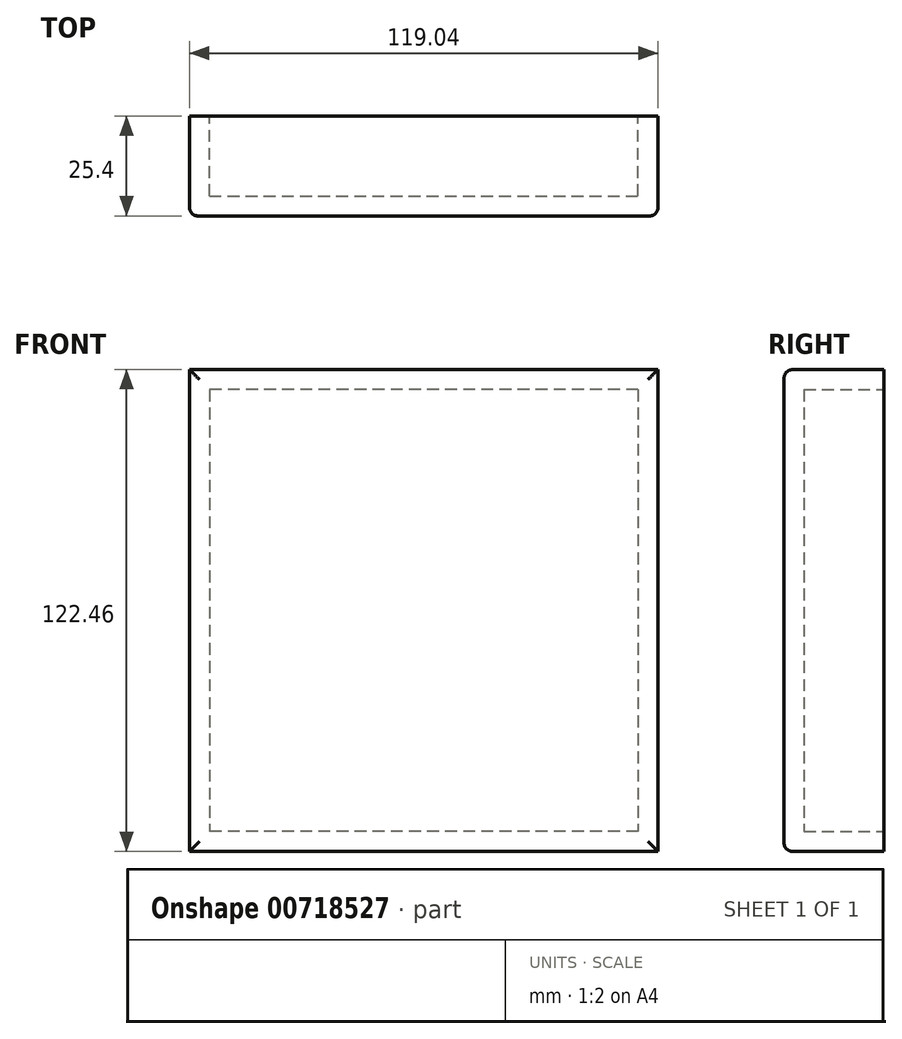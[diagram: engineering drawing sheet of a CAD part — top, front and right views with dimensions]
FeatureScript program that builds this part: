
annotation { "Feature Type Name" : "Feature", "Feature Type Description" : "" }
export const myFeature = defineFeature(function(context is Context, id is Id, definition is map)
    precondition{}
    {
        {
            var Q0;
            Q0=qCreatedBy(makeId("Front.planeOp"),FACE);
            var sketch = newSketch(context, id + "F0", { "sketchPlane" : qUnion([Q0])});
            skLineSegment(sketch, "E0.bottom", {"start": v(59.52, 61.23) * mm, "end": v(-59.52, 61.23) * mm});
            skLineSegment(sketch, "E0.top", {"start": v(59.52, -61.23) * mm, "end": v(-59.52, -61.23) * mm});
            skLineSegment(sketch, "E0.left", {"start": v(59.52, 61.23) * mm, "end": v(59.52, -61.23) * mm});
            skLineSegment(sketch, "E0.right", {"start": v(-59.52, 61.23) * mm, "end": v(-59.52, -61.23) * mm});
            skPoint(sketch, "E0.middle", {"position": v(0, 0) * mm});
            skSolve(sketch);
        }
        {
            var Q0;
            Q0=makeQuery(id+"F0.imprint","IMPRINT",FACE,{"disambiguationData":[TD([[makeQuery(id+"F0.imprint","IMPRINT",EDGE,{"derivedFrom":sQuery(id+"F0.wireOp",EDGE,"E0.bottom")}),1.0]])]});
            extrude(context, id + "F1", {"entities" : qUnion([Q0]), "depth" : 25.4 * mm, "offsetDistance" : 25.4 * mm});
        }
        {
            var Q0;
            Q0=makeQuery(id+"F1.opExtrude","CAP_EDGE",EDGE,{"disambiguationData":[OSD([sQuery(id+"F0.wireOp",EDGE,"E0.bottom")])],"isStart":false});
            var Q1;
            Q1=makeQuery(id+"F1.opExtrude","CAP_EDGE",EDGE,{"disambiguationData":[OSD([sQuery(id+"F0.wireOp",EDGE,"E0.right")])],"isStart":false});
            var Q2;
            Q2=makeQuery(id+"F1.opExtrude","CAP_EDGE",EDGE,{"disambiguationData":[OSD([sQuery(id+"F0.wireOp",EDGE,"E0.top")])],"isStart":false});
            var Q3;
            Q3=makeQuery(id+"F1.opExtrude","CAP_EDGE",EDGE,{"disambiguationData":[OSD([sQuery(id+"F0.wireOp",EDGE,"E0.left")])],"isStart":false});
            fillet(context, id + "F2", {"entities" : qUnion([Q0, Q1, Q2, Q3]), "radius" : 2.54 * mm, "tangentPropagation" : true, "rho" : 0.5, "crossSection" : FilletCrossSection.CONIC, "allowEdgeOverflow" : false});
        }
        {
            var Q0;
            Q0=makeQuery(id+"F1.opExtrude","CAP_FACE",FACE,{"disambiguationData":[OSD([sQuery(id+"F0.wireOp",EDGE,"E0.bottom"),sQuery(id+"F0.wireOp",EDGE,"E0.top"),sQuery(id+"F0.wireOp",EDGE,"E0.left"),sQuery(id+"F0.wireOp",EDGE,"E0.right")])],"isStart":true});
            shell(context, id + "F3", {"entities" : qUnion([Q0]), "thickness" : 5.08 * mm});
        }
    });
